# Revit family: ITK_Проходной адаптер_Неэкранированный
name_source: partatom
category: Обобщенные модели
units: mm (PartAtom-declared; Revit-internal decimal feet)

## family parameters
Всегда вертикально = Да
Может служить основой для арматурных стержней = Нет
На основе рабочей плоскости = Нет
Общий = Нет
При загрузке вырезать с полостями = Нет
Размер круглого соединителя = Использовать диаметр
Тип детали = Нормальный
Точка расчета площади = Нет

## types (2) — shared parameters
ADSK_URL страницы изделия = https://www.itk-group.ru
ADSK_Версия Revit = 2019
ADSK_Версия семейства = 1.0
ADSK_Группирование = I. ЩИТЫ И ПУЛЬТЫ
ADSK_Единица измерения = шт
ADSK_Завод-изготовитель = IEK
ADSK_Материал наименование = Пластик
IEK_URL = https://www.itk-group.ru
IEK_Описание = Соответствие международным стандартам качества, что обеспечивает совместимость с компонентами и с кабелем.
Изготовлены из высококачественных негорючих материалов и отличаются надежностью и удобством эксплуатации.
KSI_CMa_Строительные материалы = 01.7.14.03
KSI_CPr_Строительные изделия = 61.1.03.04
URL = https://www.iek.ru
Высота = 26 мм
Глубина = 49 мм
Изготовитель = ITK
Материал = Пластик белый
Ширина = 26 мм
zero-valued in all types: ADSK_Масса

## per-type parameters (varying)
| type | ADSK_Наименование | IEK_Цена за единицу |
| CS70-1C5EU | ITK Проходной адаптер кат.5E UTP, тип RJ45-RJ45, белый | 146.69 |
| CS70-1C06U | ITK Проходной адаптер кат. 6 UTP тип RJ45-RJ45 | 147.28 |

note: column(s) folded — value = type name in every type: ADSK_Код изделия
